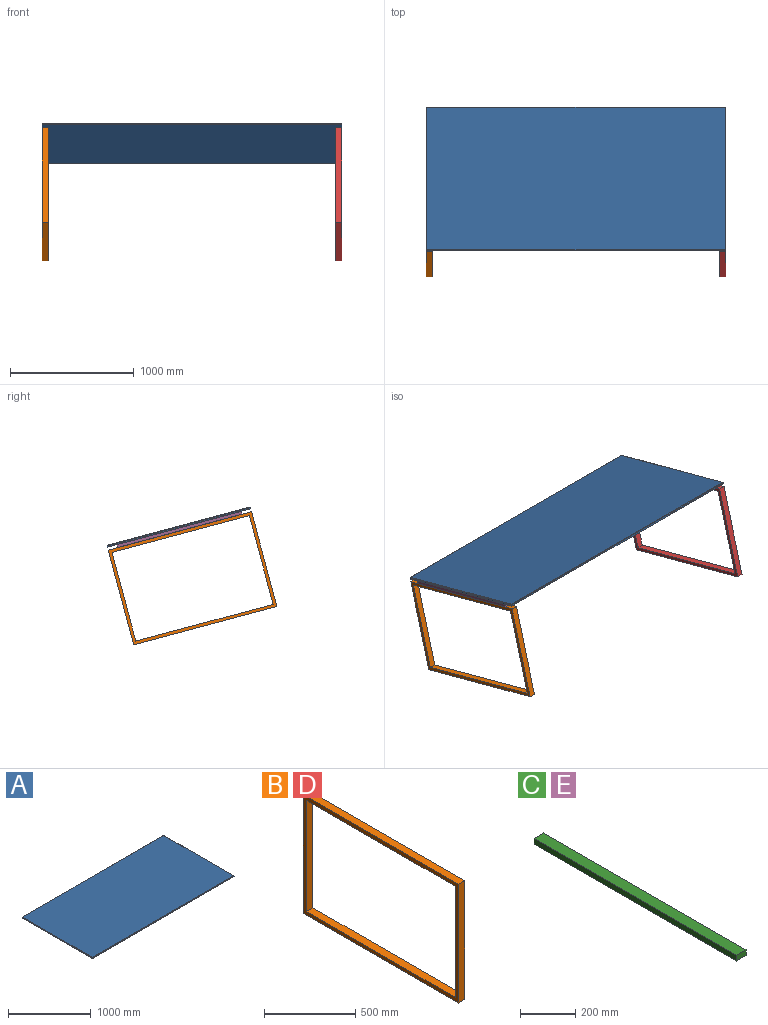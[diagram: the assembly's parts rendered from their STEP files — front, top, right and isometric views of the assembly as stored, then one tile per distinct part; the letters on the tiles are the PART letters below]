
ASSEMBLY  parts=5 mates=4
PART A: 10 faces, bbox 2425x1200x15 mm
  f0: plane 2425x10mm, normal (0,1,0), area 24250mm2, adj f2,f4,f5,f7
  f1: plane 2425x10mm, normal (0,-1,0), area 24250mm2, adj f2,f4,f5,f8
  f2: plane 1200x10mm, normal (1,0,0), area 12000mm2, adj f0,f1,f4,f6
  f3: plane 2415x1190mm, normal (0,0,1), area 2873850mm2, adj f6,f7,f8,f9
  f4: plane 2425x1200mm, normal (0,0,-1), area 2910000mm2, adj f0,f1,f2,f5
  f5: plane 1200x10mm, normal (-1,0,0), area 12000mm2, adj f0,f1,f4,f9
  f6: cylinder r=5mm len=1200mm, axis (0,-1,0), area 9396.2mm2, adj f2,f3,f7,f8
  f7: cylinder r=5mm len=2425mm, axis (1,0,0), area 19017.4mm2, adj f0,f3,f6,f9
  f8: cylinder r=5mm len=2425mm, axis (-1,0,0), area 19017.4mm2, adj f1,f3,f6,f9
  f9: cylinder r=5mm len=1200mm, axis (0,1,0), area 9396.2mm2, adj f3,f5,f7,f8
PART B: 10 faces, bbox 50x1200x794 mm
  f0: plane 1200x50mm, normal (0,0,1), area 60000mm2, adj f1,f7,f8,f9
  f1: plane 793.97x50mm, normal (0,1,0), area 39698.6mm2, adj f0,f2,f8,f9
  f2: plane 1200x50mm, normal (0,0,-1), area 60000mm2, adj f1,f7,f8,f9
  f3: plane 1150x50mm, normal (0,0,1), area 57500mm2, adj f4,f6,f8,f9
  f4: plane 743.97x50mm, normal (0,-1,0), area 37198.6mm2, adj f3,f5,f8,f9
  f5: plane 1150x50mm, normal (0,0,-1), area 57500mm2, adj f4,f6,f8,f9
  f6: plane 743.97x50mm, normal (0,1,0), area 37198.6mm2, adj f3,f5,f8,f9
  f7: plane 793.97x50mm, normal (0,-1,0), area 39698.6mm2, adj f0,f2,f8,f9
  f8: plane 1200x793.97mm, normal (1,0,0), area 97198.6mm2, adj f0,f1,f2,f3,f4,f5,f6,f7
  f9: plane 1200x793.97mm, normal (-1,0,0), area 97198.6mm2, adj f0,f1,f2,f3,f4,f5,f6,f7
PART C: 6 faces, bbox 50x1040x25 mm
  f0: plane 1040x50mm, normal (0,0,1), area 52000mm2, adj f1,f3,f4,f5
  f1: plane 50x25mm, normal (0,1,0), area 1250mm2, adj f0,f2,f4,f5
  f2: plane 1040x50mm, normal (0,0,-1), area 52000mm2, adj f1,f3,f4,f5
  f3: plane 50x25mm, normal (0,-1,0), area 1250mm2, adj f0,f2,f4,f5
  f4: plane 1040x25mm, normal (1,0,0), area 26000mm2, adj f0,f1,f2,f3
  f5: plane 1040x25mm, normal (-1,0,0), area 26000mm2, adj f0,f1,f2,f3
PART D: same geometry as B
PART E: same geometry as C
PLACE A rot(axis=(-1,0,0),15deg) t=(-378.32,263.9,-166.06)mm
PLACE B rot(axis=(-1,0,0),15deg) t=(-378.32,263.9,-166.06)mm
PLACE C rot(axis=(-1,0,0),15deg) t=(1996.68,263.9,-166.06)mm
PLACE D rot(axis=(-1,0,0),15deg) t=(1996.68,263.9,-166.06)mm
PLACE E rot(axis=(-1,0,0),15deg) t=(-378.32,263.9,-166.06)mm
MATE fastened C.f2 <-> D.f0  axis (0,-0.26,-0.97) through (796.68,257.42,-190.2)mm
MATE fastened E.f2 <-> B.f0  axis (0,-0.26,-0.97) through (-1578.32,257.42,-190.2)mm
MATE fastened A.f4 <-> C.f0  axis (0,-0.26,-0.97) through (821.68,263.9,-166.06)mm
MATE fastened A.f4 <-> E.f0  axis (0,-0.26,-0.97) through (-1603.32,263.9,-166.06)mm
